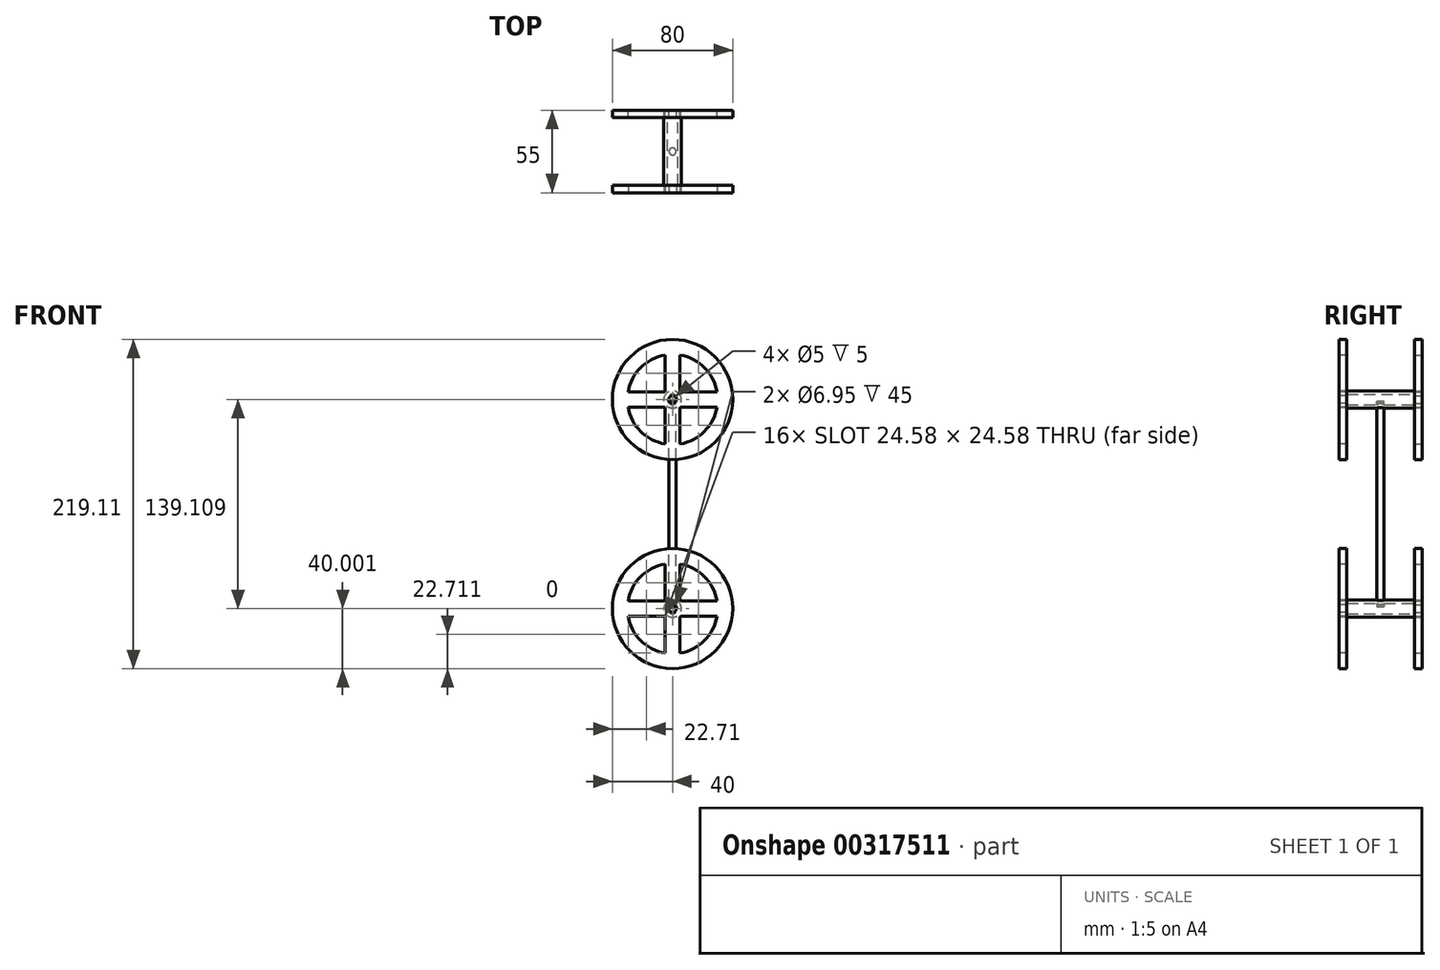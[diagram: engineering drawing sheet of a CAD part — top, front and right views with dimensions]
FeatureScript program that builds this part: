
annotation { "Feature Type Name" : "Feature", "Feature Type Description" : "" }
export const myFeature = defineFeature(function(context is Context, id is Id, definition is map)
    precondition{}
    {
        {
            var Q0;
            Q0=qCreatedBy(makeId("Front.planeOp"),FACE);
            var sketch = newSketch(context, id + "F0", { "sketchPlane" : qUnion([Q0])});
            skCircle(sketch, "E0", {"center": v(0, 0) * mm, "radius": 40 * mm});
            skArc(sketch, "E1", {"start": v(29.58, 5) * mm, "mid": v(21.21, 21.21) * mm, "end": v(5, 29.58) * mm});
            skArc(sketch, "E2", {"start": v(-5.6, -5) * mm, "mid": v(-5.3, -5.3) * mm, "end": v(-5, -5.6) * mm});
            skCircle(sketch, "E3", {"center": v(0, 0) * mm, "radius": 2.5 * mm});
            skLineSegment(sketch, "E4", {"start": v(0, 7.5) * mm, "end": v(0, 30) * mm, "construction": true});
            skLineSegment(sketch, "E5", {"start": v(0, -2.5) * mm, "end": v(0, -30) * mm});
            skLineSegment(sketch, "E6", {"start": v(-7.5, 0) * mm, "end": v(-30, 0) * mm, "construction": true});
            skLineSegment(sketch, "E7", {"start": v(0, 0) * mm, "end": v(0, 2.5) * mm, "construction": true});
            skLineSegment(sketch, "E8", {"start": v(0, 0) * mm, "end": v(2.5, 0) * mm, "construction": true});
            skLineSegment(sketch, "E9", {"start": v(0, 0) * mm, "end": v(0, -30) * mm, "construction": true});
            skLineSegment(sketch, "E10", {"start": v(0, 0) * mm, "end": v(-2.5, 0) * mm, "construction": true});
            skLineSegment(sketch, "E11.0", {"start": v(-5, 5.6) * mm, "end": v(-5, 29.58) * mm});
            skLineSegment(sketch, "E12.0", {"start": v(5, 5.6) * mm, "end": v(5, 29.58) * mm});
            skLineSegment(sketch, "E13.0", {"start": v(5.6, 5) * mm, "end": v(29.58, 5) * mm});
            skLineSegment(sketch, "E14.0", {"start": v(5, -5.6) * mm, "end": v(5, -29.58) * mm});
            skLineSegment(sketch, "E15.0", {"start": v(-5, -5.6) * mm, "end": v(-5, -29.58) * mm});
            skLineSegment(sketch, "E16.0", {"start": v(-5.6, -5) * mm, "end": v(-29.58, -5) * mm});
            skLineSegment(sketch, "E17.0", {"start": v(-5.6, 5) * mm, "end": v(-29.58, 5) * mm});
            skArc(sketch, "E18.trimOffspring", {"start": v(-29.58, -5) * mm, "mid": v(-21.21, -21.21) * mm, "end": v(-5, -29.58) * mm});
            skLineSegment(sketch, "E19.trimOffspring", {"start": v(-7.5, 0) * mm, "end": v(-30, 0) * mm});
            skLineSegment(sketch, "E20.trimOffspring", {"start": v(7.5, 0) * mm, "end": v(30, 0) * mm, "construction": true});
            skLineSegment(sketch, "E21.trimOffspring", {"start": v(0, 7.5) * mm, "end": v(0, 30) * mm});
            skArc(sketch, "E22.trimOffspring", {"start": v(5, -5.6) * mm, "mid": v(5.3, -5.3) * mm, "end": v(5.6, -5) * mm});
            skArc(sketch, "E23.trimOffspring", {"start": v(5.6, 5) * mm, "mid": v(5.3, 5.3) * mm, "end": v(5, 5.6) * mm});
            skArc(sketch, "E24.trimOffspring", {"start": v(-5, 5.6) * mm, "mid": v(-5.3, 5.3) * mm, "end": v(-5.6, 5) * mm});
            skLineSegment(sketch, "E25.0", {"start": v(5.6, -5) * mm, "end": v(29.58, -5) * mm});
            skArc(sketch, "E26.trimOffspring", {"start": v(-5, 29.58) * mm, "mid": v(-21.21, 21.21) * mm, "end": v(-29.58, 5) * mm});
            skArc(sketch, "E27.trimOffspring", {"start": v(5, -29.58) * mm, "mid": v(21.21, -21.21) * mm, "end": v(29.58, -5) * mm});
            skSolve(sketch);
        }
        {
            var Q0;
            Q0=qSketchRegion(id+"F0",true);
            extrude(context, id + "F1", {"entities" : qUnion([Q0]), "endBound" : BoundingType.SYMMETRIC, "depth" : 5 * mm});
        }
        {
            var Q0;
            Q0=qCreatedBy(makeId("Front.planeOp"),FACE);
            var sketch = newSketch(context, id + "F2", { "sketchPlane" : qUnion([Q0])});
            skCircle(sketch, "E28", {"center": v(0, 0) * mm, "radius": 3.47 * mm});
            skCircle(sketch, "E29", {"center": v(0, 0) * mm, "radius": 5.81 * mm});
            skSolve(sketch);
        }
        {
            var Q0;
            Q0 = qSketchRegion(id + "F2", true);
            extrude(context, id + "F3", {"entities" : qUnion([Q0]), "operationType" : NewBodyOperationType.ADD, "depth" : 25 * mm});
        }
        {
            var Q0;
            Q0=makeQuery(id+"F1.opExtrude","SWEPT_BODY",BODY,{"disambiguationData":[OSD([sQuery(id+"F0.wireOp",EDGE,"E0"),sQuery(id+"F0.wireOp",EDGE,"E1"),sQuery(id+"F0.wireOp",EDGE,"E2"),sQuery(id+"F0.wireOp",EDGE,"E3"),sQuery(id+"F0.wireOp",EDGE,"E11.0"),sQuery(id+"F0.wireOp",EDGE,"E12.0"),sQuery(id+"F0.wireOp",EDGE,"E13.0"),sQuery(id+"F0.wireOp",EDGE,"E14.0"),sQuery(id+"F0.wireOp",EDGE,"E15.0"),sQuery(id+"F0.wireOp",EDGE,"E16.0"),sQuery(id+"F0.wireOp",EDGE,"E17.0"),sQuery(id+"F0.wireOp",EDGE,"E18.trimOffspring"),sQuery(id+"F0.wireOp",EDGE,"E22.trimOffspring"),sQuery(id+"F0.wireOp",EDGE,"E23.trimOffspring"),sQuery(id+"F0.wireOp",EDGE,"E24.trimOffspring"),sQuery(id+"F0.wireOp",EDGE,"E25.0"),sQuery(id+"F0.wireOp",EDGE,"E26.trimOffspring"),sQuery(id+"F0.wireOp",EDGE,"E27.trimOffspring")])]});
            var Q1;
            Q1=makeQuery(id+"F3.opExtrude","CAP_FACE",FACE,{"disambiguationData":[OSD([sQuery(id+"F2.wireOp",EDGE,"E28"),sQuery(id+"F2.wireOp",EDGE,"E29")])],"isStart":false});
            mirror(context, id + "F4", {"operationType" : NewBodyOperationType.ADD, "entities" : qUnion([Q0]), "mirrorPlane" : qUnion([Q1])});
        }
        {
            var Q0;
            Q0=qCreatedBy(makeId("Front.planeOp"),FACE);
            cPlane(context, id + "F5", {"entities" : qUnion([Q0]), "cplaneType" : CPlaneType.OFFSET, "offset" : 25 * mm, "width" : 150 * mm, "height" : 150 * mm});
        }
        {
            var Q0;
            Q0=qCreatedBy(id+"F5.planeOp",FACE);
            var sketch = newSketch(context, id + "F6", { "sketchPlane" : qUnion([Q0])});
            skLineSegment(sketch, "E30.top", {"start": v(0, -69.55) * mm, "end": v(2.35, -69.55) * mm});
            skLineSegment(sketch, "E30.left", {"start": v(0, -2.64) * mm, "end": v(0, -69.55) * mm});
            skLineSegment(sketch, "E30.right", {"start": v(2.35, -2.64) * mm, "end": v(2.35, -69.55) * mm});
            skArc(sketch, "E31", {"start": v(0, -2.64) * mm, "mid": v(1.37, -2.26) * mm, "end": v(2.35, -1.21) * mm});
            skLineSegment(sketch, "E32", {"start": v(2.35, -2.64) * mm, "end": v(2.35, -1.21) * mm});
            skSolve(sketch);
        }
        {
            var Q0;
            Q0 = qSketchRegion(id + "F6", true);
            var Q1;
            Q1=sQuery(id+"F6.wireOp",EDGE,"E30.left");
            revolve(context, id + "F7", {"operationType" : NewBodyOperationType.ADD, "entities" : qUnion([Q0]), "axis" : qUnion([Q1]), "revolveType" : RevolveType.FULL});
        }
        {
            var Q0;
            Q0=makeQuery(id+"F1.opExtrude","SWEPT_BODY",BODY,{"disambiguationData":[OSD([sQuery(id+"F0.wireOp",EDGE,"E0"),sQuery(id+"F0.wireOp",EDGE,"E1"),sQuery(id+"F0.wireOp",EDGE,"E2"),sQuery(id+"F0.wireOp",EDGE,"E3"),sQuery(id+"F0.wireOp",EDGE,"E11.0"),sQuery(id+"F0.wireOp",EDGE,"E12.0"),sQuery(id+"F0.wireOp",EDGE,"E13.0"),sQuery(id+"F0.wireOp",EDGE,"E14.0"),sQuery(id+"F0.wireOp",EDGE,"E15.0"),sQuery(id+"F0.wireOp",EDGE,"E16.0"),sQuery(id+"F0.wireOp",EDGE,"E17.0"),sQuery(id+"F0.wireOp",EDGE,"E18.trimOffspring"),sQuery(id+"F0.wireOp",EDGE,"E22.trimOffspring"),sQuery(id+"F0.wireOp",EDGE,"E23.trimOffspring"),sQuery(id+"F0.wireOp",EDGE,"E24.trimOffspring"),sQuery(id+"F0.wireOp",EDGE,"E25.0"),sQuery(id+"F0.wireOp",EDGE,"E26.trimOffspring"),sQuery(id+"F0.wireOp",EDGE,"E27.trimOffspring")])]});
            var Q1;
            Q1=makeQuery(id+"F7.opRevolve","SWEPT_FACE",FACE,{"disambiguationData":[OSD([sQuery(id+"F6.wireOp",EDGE,"E30.top")])]});
            mirror(context, id + "F8", {"operationType" : NewBodyOperationType.ADD, "entities" : qUnion([Q0]), "mirrorPlane" : qUnion([Q1])});
        }
    });
